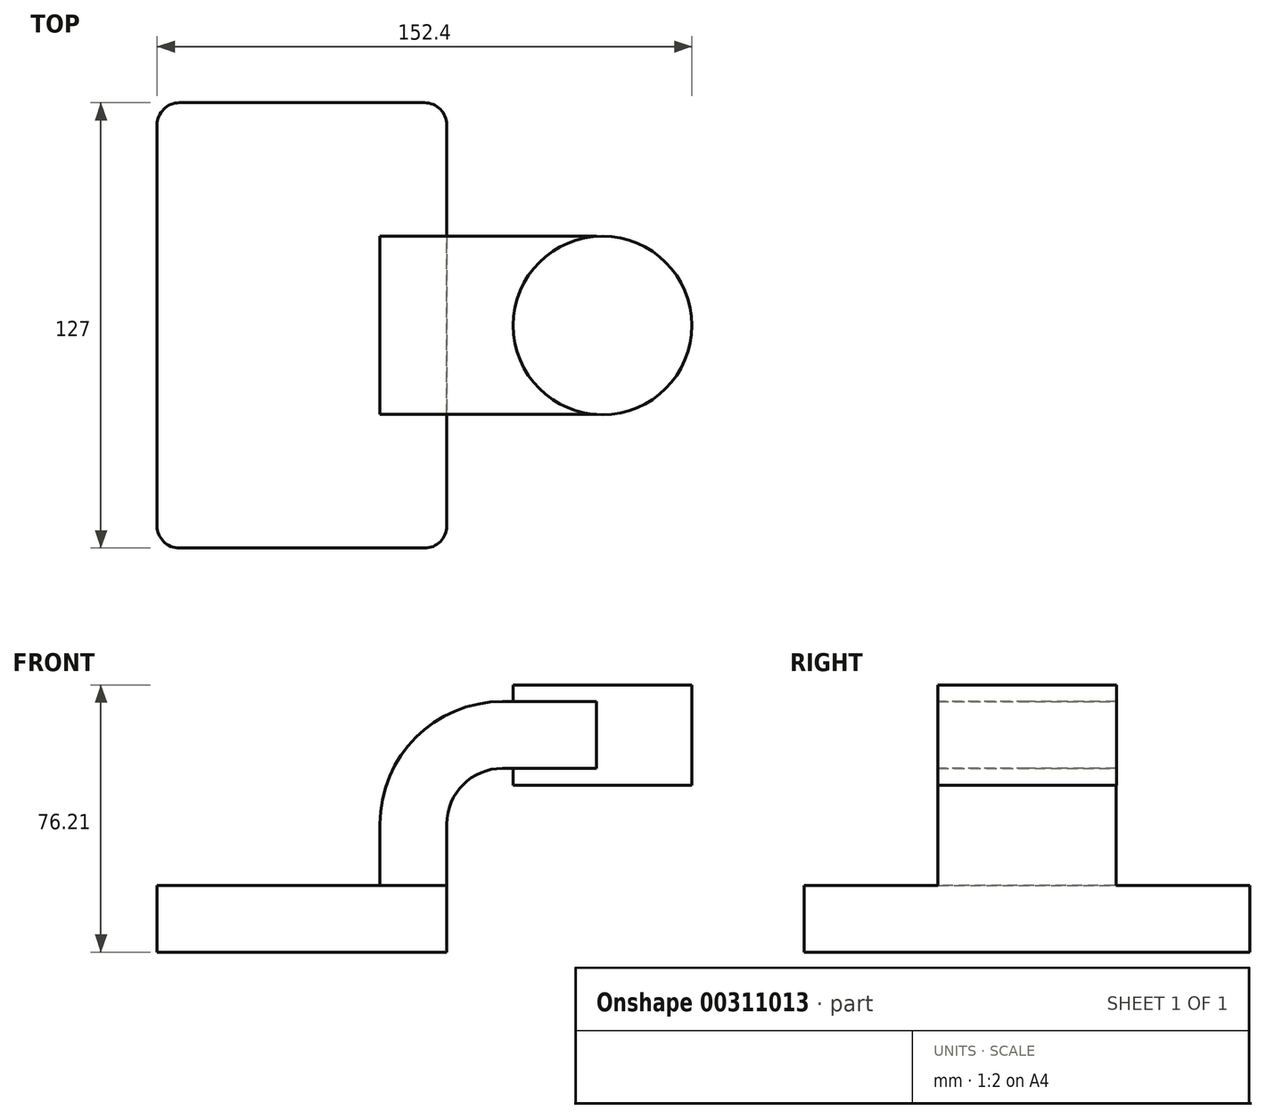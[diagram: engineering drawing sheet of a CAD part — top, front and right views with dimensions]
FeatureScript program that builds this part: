
annotation { "Feature Type Name" : "Feature", "Feature Type Description" : "" }
export const myFeature = defineFeature(function(context is Context, id is Id, definition is map)
    precondition{}
    {
        {
            var Q0;
            Q0=qCreatedBy(makeId("Front.planeOp"),FACE);
            var sketch = newSketch(context, id + "F0", { "sketchPlane" : qUnion([Q0])});
            skLineSegment(sketch, "E0.bottom", {"start": v(41.28, -9.52) * mm, "end": v(-41.28, -9.53) * mm});
            skLineSegment(sketch, "E0.top", {"start": v(41.28, 9.53) * mm, "end": v(-41.28, 9.53) * mm});
            skLineSegment(sketch, "E0.left", {"start": v(41.28, -9.52) * mm, "end": v(41.28, 9.53) * mm});
            skLineSegment(sketch, "E0.right", {"start": v(-41.28, -9.53) * mm, "end": v(-41.28, 9.53) * mm});
            skPoint(sketch, "E0.middle", {"position": v(0, 0) * mm});
            skLineSegment(sketch, "E1.bottom", {"start": v(111.12, 38.1) * mm, "end": v(60.32, 38.1) * mm});
            skLineSegment(sketch, "E1.top", {"start": v(111.12, 66.67) * mm, "end": v(60.32, 66.67) * mm});
            skLineSegment(sketch, "E1.left", {"start": v(111.12, 38.1) * mm, "end": v(111.12, 66.67) * mm});
            skLineSegment(sketch, "E1.right", {"start": v(60.32, 38.1) * mm, "end": v(60.32, 66.67) * mm});
            skPoint(sketch, "E1.middle", {"position": v(85.72, 52.39) * mm});
            skLineSegment(sketch, "E2", {"start": v(41.28, 9.53) * mm, "end": v(41.28, 27) * mm});
            skArc(sketch, "E3", {"start": v(41.27, 27) * mm, "mid": v(45.92, 38.23) * mm, "end": v(57.15, 42.88) * mm});
            skLineSegment(sketch, "E4", {"start": v(57.15, 42.88) * mm, "end": v(85.66, 42.88) * mm});
            skLineSegment(sketch, "E5.0", {"start": v(57.15, 61.93) * mm, "end": v(85.66, 61.93) * mm});
            skArc(sketch, "E5.1", {"start": v(22.22, 27) * mm, "mid": v(32.45, 51.7) * mm, "end": v(57.15, 61.93) * mm});
            skLineSegment(sketch, "E5.2", {"start": v(22.22, 9.53) * mm, "end": v(22.22, 27) * mm});
            skLineSegment(sketch, "E6", {"start": v(85.66, 38.1) * mm, "end": v(85.66, 66.67) * mm});
            skFitSpline(sketch, "E7", {"points": [v(-41.28, 9.53) * mm, v(57.15, 61.93) * mm], "startDerivative": vector(40.4, 129.1) * mm, "endDerivative": vector(171.45, -6.53) * mm});
            skSolve(sketch);
        }
        {
            var Q0;
            Q0=makeQuery(id+"F0.imprint","IMPRINT",FACE,{"disambiguationData":[TD([[makeQuery(id+"F0.imprint","IMPRINT",EDGE,{"derivedFrom":sQuery(id+"F0.wireOp",EDGE,"E0.bottom")}),-1.0]])]});
            extrude(context, id + "F1", {"entities" : qUnion([Q0]), "endBound" : BoundingType.SYMMETRIC, "oppositeDirection" : true, "depth" : 127 * mm});
        }
        {
            var Q0;
            {var subQ1=sQuery(id+"F0.wireOp",EDGE,"E2");Q0=makeQuery(id+"F0.imprint","IMPRINT",FACE,{"disambiguationData":[TD([[makeQuery(id+"F0.imprint","IMPRINT",EDGE,{"derivedFrom":subQ1}),1.0]])]});}
            var Q1;
            {var subQ0=sQuery(id+"F0.wireOp",EDGE,"E4");var subQ1=sQuery(id+"F0.wireOp",EDGE,"E1.right");var subQ2=makeQuery(id+"F0.imprint","INTERSECT",VERTEX,{"derivedFrom":[subQ1,subQ0]});Q1=makeQuery(id+"F0.imprint","IMPRINT",FACE,{"disambiguationData":[TD([[makeQuery(id+"F0.imprint","IMPRINT",EDGE,{"disambiguationData":[TD([[subQ2,-1.0]])],"derivedFrom":subQ1}),-1.0]])]});}
            extrude(context, id + "F2", {"entities" : qUnion([Q0, Q1]), "operationType" : NewBodyOperationType.ADD, "endBound" : BoundingType.SYMMETRIC, "depth" : 50.8 * mm});
        }
        {
            var Q0;
            Q0=makeQuery(id+"F0.imprint","IMPRINT",FACE,{"disambiguationData":[TD([[makeQuery(id+"F0.imprint","IMPRINT",EDGE,{"derivedFrom":sQuery(id+"F0.wireOp",EDGE,"E5.1")}),1.0]])]});
            extrude(context, id + "F3", {"entities" : qUnion([Q0]), "operationType" : NewBodyOperationType.ADD, "endBound" : BoundingType.SYMMETRIC, "depth" : 15.88 * mm});
        }
        {
            var Q0;
            {var subQ4=sQuery(id+"F0.wireOp",EDGE,"E1.left");Q0=makeQuery(id+"F0.imprint","IMPRINT",FACE,{"disambiguationData":[TD([[makeQuery(id+"F0.imprint","IMPRINT",EDGE,{"derivedFrom":subQ4}),1.0]])]});}
            var Q1;
            Q1=sQuery(id+"F0.wireOp",EDGE,"E6");
            revolve(context, id + "F4", {"operationType" : NewBodyOperationType.ADD, "entities" : qUnion([Q0]), "axis" : qUnion([Q1]), "revolveType" : RevolveType.FULL});
        }
        {
            var Q0;
            Q0=makeQuery(id+"F1.opExtrude","CAP_EDGE",EDGE,{"disambiguationData":[OSD([sQuery(id+"F0.wireOp",EDGE,"E0.right")])],"isStart":true});
            var Q1;
            Q1=makeQuery(id+"F1.opExtrude","CAP_EDGE",EDGE,{"disambiguationData":[OSD([sQuery(id+"F0.wireOp",EDGE,"E0.left")])],"isStart":true});
            var Q2;
            Q2=makeQuery(id+"F1.opExtrude","CAP_EDGE",EDGE,{"disambiguationData":[OSD([sQuery(id+"F0.wireOp",EDGE,"E0.left")])],"isStart":false});
            var Q3;
            Q3=makeQuery(id+"F1.opExtrude","CAP_EDGE",EDGE,{"disambiguationData":[OSD([sQuery(id+"F0.wireOp",EDGE,"E0.right")])],"isStart":false});
            fillet(context, id + "F5", {"entities" : qUnion([Q0, Q1, Q2, Q3]), "radius" : 6.35 * mm, "tangentPropagation" : true, "allowEdgeOverflow" : false});
        }
    });
